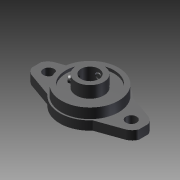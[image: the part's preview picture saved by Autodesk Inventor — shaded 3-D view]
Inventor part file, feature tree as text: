
AUTODESK INVENTOR PART (.ipt)
format: ipt  version: 2011 SP1 (Build 150282100, 282)  size: 219,648 bytes
history: native  units: mm
features: sketch x10, other x7, revolve x6, extrude x4
ambient origin geometry x8: Origin, YZ Plane, XZ Plane, XY Plane, X Axis, Y Axis, Z Axis, Center Point
bodies: Solid1 (feature_tree)
feature tree (27):
  extrude  "Extrusion1"  TaperAngle=360.0deg  [1 undecoded]
  revolve  "Revolution1"  Angle=360.0deg
  extrude  "Extrusion2"  TaperAngle=360.0deg  [1 undecoded]
  revolve  "Revolution2"  Angle=360.0deg
  revolve  "Revolution3"  [1 undecoded]
  revolve  "Revolution4"  [1 undecoded]
  revolve  "Revolution5"  [1 undecoded]
  revolve  "Revolution6"  [1 undecoded]
  extrude  "Extrusion3"  [1 undecoded]
  extrude  "Extrusion4"  [1 undecoded]
  other  "housing_XY"
  other  "housing_YZ"
  other  "housing_ZX"
  other  "housing_X"
  other  "housing_Y"
  other  "housing_Z"
  other  "housing_Center"
  sketch  "Sketch_1"  dims[d0=4.0mm d1=0.0mm d2=360.0deg]
  sketch  "Sketch_2"  dims[d3=1.0mm d4=0.0mm d5=360.0deg]
  sketch  "Sketch_5"  dims[d6=360.0deg d7=360.0deg]
  sketch  "Sketch_6"  dims[d8=360.0deg d9=360.0deg]
  sketch  "Sketch_7"  dims[d10=1.5mm d11=0.0mm d12=1.5mm d13=0.0mm]
  sketch  "Sketch_8"  dims[d14=0.0mm]
  sketch  "Sketch_9"
  sketch  "Sketch_10"
  sketch  "Sketch_11"
  sketch  "Sketch_12"
note: 8 required parameter values undecoded (feature->parameter linkage not recoverable at this tier; creation-order binding heuristic only, values carry confidence <= 0.55)